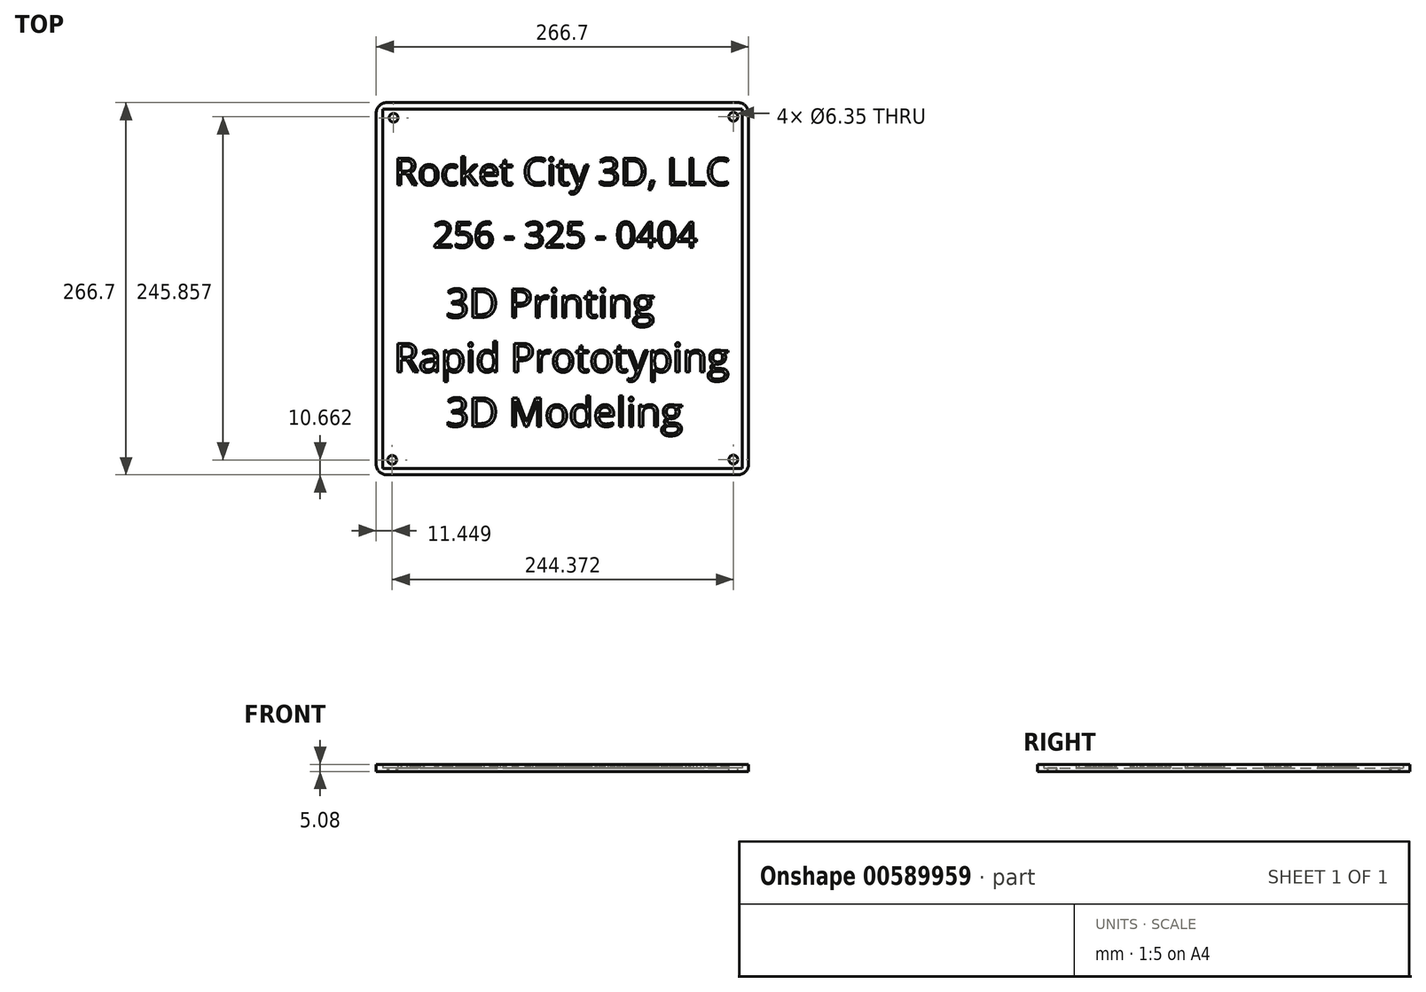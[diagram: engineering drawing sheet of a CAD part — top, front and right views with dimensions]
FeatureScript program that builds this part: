
annotation { "Feature Type Name" : "Feature", "Feature Type Description" : "" }
export const myFeature = defineFeature(function(context is Context, id is Id, definition is map)
    precondition{}
    {
        {
            var Q0;
            Q0=qCreatedBy(makeId("Top.planeOp"),FACE);
            var sketch = newSketch(context, id + "F0", { "sketchPlane" : qUnion([Q0])});
            skLineSegment(sketch, "E0.bottom", {"start": v(133.35, -133.35) * mm, "end": v(-133.35, -133.35) * mm});
            skLineSegment(sketch, "E0.top", {"start": v(133.35, 133.35) * mm, "end": v(-133.35, 133.35) * mm});
            skLineSegment(sketch, "E0.left", {"start": v(133.35, -133.35) * mm, "end": v(133.35, 133.35) * mm});
            skLineSegment(sketch, "E0.right", {"start": v(-133.35, -133.35) * mm, "end": v(-133.35, 133.35) * mm});
            skPoint(sketch, "E0.middle", {"position": v(0, 0) * mm});
            skSolve(sketch);
        }
        {
            var Q0;
            Q0=makeQuery(id+"F0.imprint","IMPRINT",FACE,{"disambiguationData":[TD([[makeQuery(id+"F0.imprint","IMPRINT",EDGE,{"derivedFrom":sQuery(id+"F0.wireOp",EDGE,"E0.bottom")}),-1.0]])]});
            extrude(context, id + "F1", {"entities" : qUnion([Q0]), "depth" : 2.54 * mm, "offsetDistance" : 25.4 * mm});
        }
        {
            var Q0;
            Q0=makeQuery(id+"F1.opExtrude","CAP_FACE",FACE,{"disambiguationData":[OSD([sQuery(id+"F0.wireOp",EDGE,"E0.bottom"),sQuery(id+"F0.wireOp",EDGE,"E0.top"),sQuery(id+"F0.wireOp",EDGE,"E0.left"),sQuery(id+"F0.wireOp",EDGE,"E0.right")])],"isStart":false});
            var sketch = newSketch(context, id + "F2", { "sketchPlane" : qUnion([Q0])});
            skLineSegment(sketch, "E1.0", {"start": v(128.78, -128.78) * mm, "end": v(128.78, 128.78) * mm});
            skLineSegment(sketch, "E1.1", {"start": v(128.78, -128.78) * mm, "end": v(-128.78, -128.78) * mm});
            skLineSegment(sketch, "E1.2", {"start": v(-128.78, -128.78) * mm, "end": v(-128.78, 128.78) * mm});
            skLineSegment(sketch, "E1.3", {"start": v(128.78, 128.78) * mm, "end": v(-128.78, 128.78) * mm});
            skSolve(sketch);
        }
        {
            var Q0;
            Q0=makeQuery(id+"F2.imprint","IMPRINT",FACE,{"disambiguationData":[TD([[makeQuery(id+"F2.imprint","IMPRINT",EDGE,{"derivedFrom":sQuery(id+"F2.wireOp",EDGE,"E1.0")}),-1.0]])]});
            extrude(context, id + "F3", {"entities" : qUnion([Q0]), "operationType" : NewBodyOperationType.ADD, "depth" : 2.54 * mm, "offsetDistance" : 25.4 * mm});
        }
        {
            var Q0;
            Q0=makeQuery(id+"F1.opExtrude","CAP_FACE",FACE,{"disambiguationData":[OSD([sQuery(id+"F0.wireOp",EDGE,"E0.bottom"),sQuery(id+"F0.wireOp",EDGE,"E0.top"),sQuery(id+"F0.wireOp",EDGE,"E0.left"),sQuery(id+"F0.wireOp",EDGE,"E0.right")])],"isStart":false});
            var sketch = newSketch(context, id + "F4", { "sketchPlane" : qUnion([Q0])});
            skText(sketch, "E2", { "text": "Rocket City 3D, LLC\n", "fontName": "OpenSans-Regular.ttf"});
            skText(sketch, "E3", { "text": "256 - 325 - 0404", "fontName": "OpenSans-Regular.ttf"});
            skText(sketch, "E4", { "text": "     3D Printing\nRapid Prototyping\n     3D Modeling\n", "fontName": "OpenSans-Regular.ttf"});
            const initialGuessF4  = {"E2": [-0.12039, 0.0742, 1, 0, 0.0195], "E3": [-0.09267, 0.02944, 1, 0, 0.01842], "E4": [-0.12065, -0.02066, 1, 0, 0.02066]};
            skSetInitialGuess(sketch, initialGuessF4);
            skSolve(sketch);
        }
        {
            var Q0;
            Q0 = qSketchRegion(id + "F4", true);
            extrude(context, id + "F5", {"entities" : qUnion([Q0]), "operationType" : NewBodyOperationType.ADD, "depth" : 2.54 * mm, "offsetDistance" : 25.4 * mm});
        }
        {
            var Q0;
            {var subQ0=sQuery(id+"F0.wireOp",EDGE,"E0.right");var subQ1=sQuery(id+"F0.wireOp",EDGE,"E0.top");Q0=makeQuery(id+"F3.boolean.opBoolean","MERGE",EDGE,{"derivedFrom":[makeQuery(id+"F1.opExtrude","SWEPT_EDGE",EDGE,{"disambiguationData":[OSD([subQ1,subQ0])]}),makeQuery(id+"F3.opExtrude","SWEPT_EDGE",EDGE,{"disambiguationData":[OSD([subQ1,subQ0])]})]});}
            var Q1;
            {var subQ0=sQuery(id+"F0.wireOp",EDGE,"E0.left");var subQ1=sQuery(id+"F0.wireOp",EDGE,"E0.top");Q1=makeQuery(id+"F3.boolean.opBoolean","MERGE",EDGE,{"derivedFrom":[makeQuery(id+"F1.opExtrude","SWEPT_EDGE",EDGE,{"disambiguationData":[OSD([subQ1,subQ0])]}),makeQuery(id+"F3.opExtrude","SWEPT_EDGE",EDGE,{"disambiguationData":[OSD([subQ1,subQ0])]})]});}
            var Q2;
            {var subQ0=sQuery(id+"F0.wireOp",EDGE,"E0.left");var subQ1=sQuery(id+"F0.wireOp",EDGE,"E0.bottom");Q2=makeQuery(id+"F3.boolean.opBoolean","MERGE",EDGE,{"derivedFrom":[makeQuery(id+"F1.opExtrude","SWEPT_EDGE",EDGE,{"disambiguationData":[OSD([subQ1,subQ0])]}),makeQuery(id+"F3.opExtrude","SWEPT_EDGE",EDGE,{"disambiguationData":[OSD([subQ1,subQ0])]})]});}
            var Q3;
            {var subQ0=sQuery(id+"F0.wireOp",EDGE,"E0.right");var subQ1=sQuery(id+"F0.wireOp",EDGE,"E0.bottom");Q3=makeQuery(id+"F3.boolean.opBoolean","MERGE",EDGE,{"derivedFrom":[makeQuery(id+"F1.opExtrude","SWEPT_EDGE",EDGE,{"disambiguationData":[OSD([subQ1,subQ0])]}),makeQuery(id+"F3.opExtrude","SWEPT_EDGE",EDGE,{"disambiguationData":[OSD([subQ1,subQ0])]})]});}
            fillet(context, id + "F6", {"entities" : qUnion([Q0, Q1, Q2, Q3]), "radius" : 7.62 * mm, "tangentPropagation" : true, "allowEdgeOverflow" : false});
        }
        {
            var Q0;
            Q0=makeQuery(id+"F5.boolean.opBoolean","SPLIT",FACE,{"disambiguationData":[TD([makeQuery(id+"F3.opExtrude","SWEPT_FACE",FACE,{"disambiguationData":[OSD([sQuery(id+"F2.wireOp",EDGE,"E1.0")])]})])],"derivedFrom":makeQuery(id+"F1.opExtrude","CAP_FACE",FACE,{"disambiguationData":[OSD([sQuery(id+"F0.wireOp",EDGE,"E0.bottom"),sQuery(id+"F0.wireOp",EDGE,"E0.top"),sQuery(id+"F0.wireOp",EDGE,"E0.left"),sQuery(id+"F0.wireOp",EDGE,"E0.right")])],"isStart":false})});
            var sketch = newSketch(context, id + "F7", { "sketchPlane" : qUnion([Q0])});
            skCircle(sketch, "E5", {"center": v(-120.9, 122.43) * mm, "radius": 3.18 * mm});
            skCircle(sketch, "E6", {"center": v(122.47, 123.17) * mm, "radius": 3.18 * mm});
            skCircle(sketch, "E7", {"center": v(-121.9, -122.69) * mm, "radius": 3.18 * mm});
            skCircle(sketch, "E8", {"center": v(122.43, -122.43) * mm, "radius": 3.18 * mm});
            skSolve(sketch);
        }
        {
            var Q0;
            Q0 = qSketchRegion(id + "F7", true);
            extrude(context, id + "F8", {"entities" : qUnion([Q0]), "operationType" : NewBodyOperationType.REMOVE, "endBound" : BoundingType.THROUGH_ALL, "oppositeDirection" : true, "depth" : 25.4 * mm, "offsetDistance" : 25.4 * mm});
        }
    });
